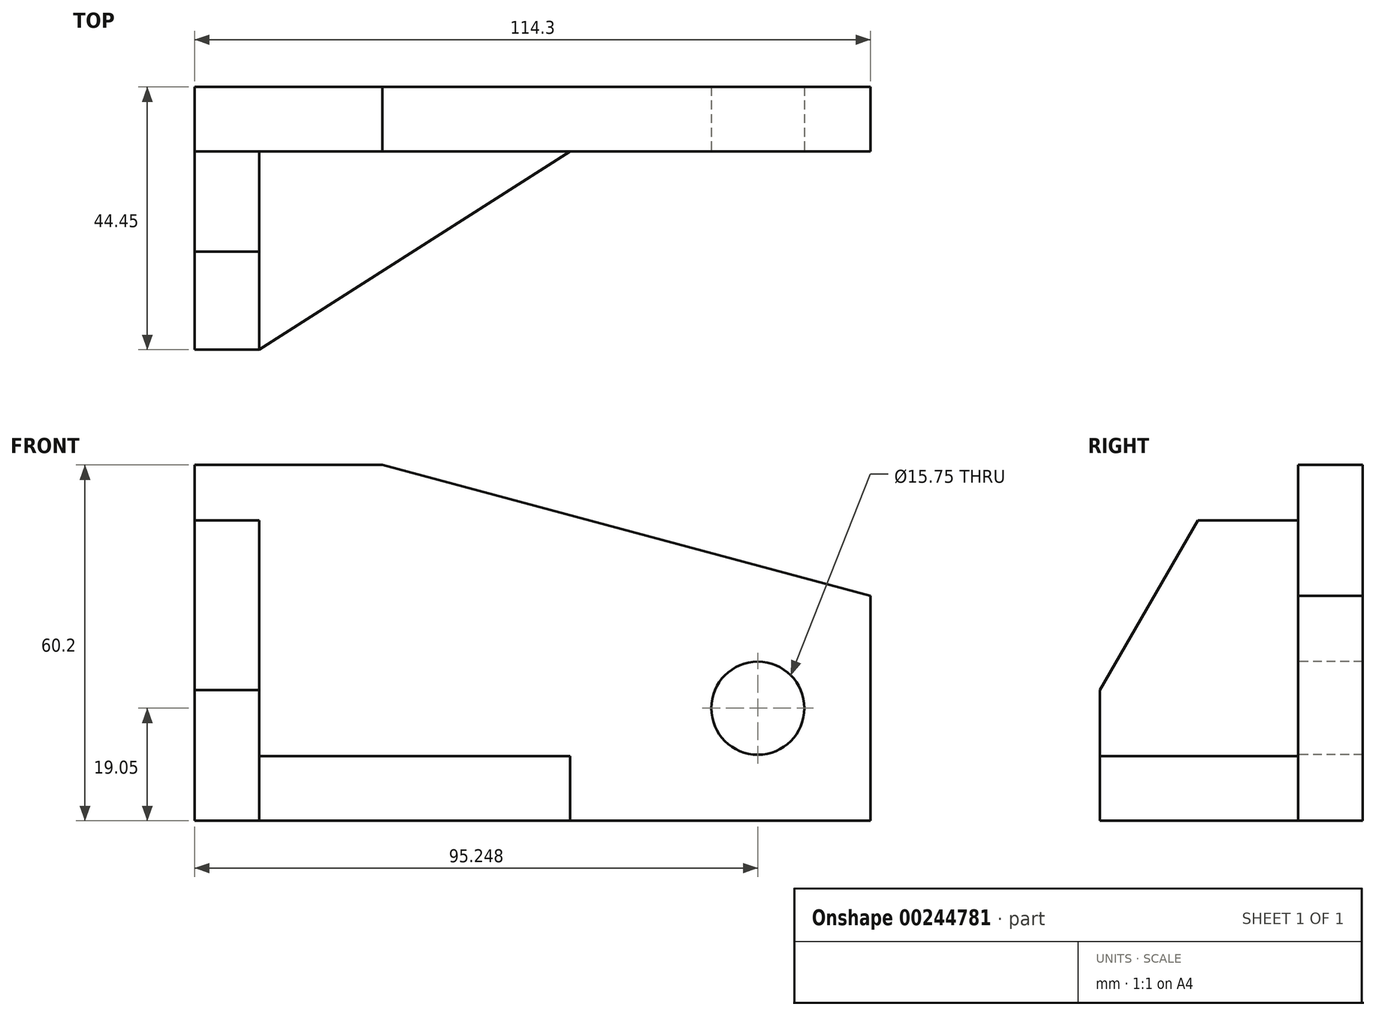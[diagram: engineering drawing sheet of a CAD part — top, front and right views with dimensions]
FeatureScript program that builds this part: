
annotation { "Feature Type Name" : "Feature", "Feature Type Description" : "" }
export const myFeature = defineFeature(function(context is Context, id is Id, definition is map)
    precondition{}
    {
        {
            var Q0;
            Q0=qCreatedBy(makeId("Front.planeOp"),FACE);
            var sketch = newSketch(context, id + "F0", { "sketchPlane" : qUnion([Q0])});
            skLineSegment(sketch, "E0.bottom", {"start": v(-10.92, 60.2) * mm, "end": v(20.83, 60.2) * mm});
            skLineSegment(sketch, "E0.top", {"start": v(-10.92, 0) * mm, "end": v(20.83, 0) * mm});
            skLineSegment(sketch, "E0.left", {"start": v(-10.92, 60.2) * mm, "end": v(-10.92, 0) * mm});
            skLineSegment(sketch, "E1", {"start": v(20.83, 60.2) * mm, "end": v(103.38, 38.08) * mm});
            skLineSegment(sketch, "E2", {"start": v(20.83, 0) * mm, "end": v(103.38, 0) * mm});
            skLineSegment(sketch, "E3", {"start": v(103.38, 38.08) * mm, "end": v(103.38, 0) * mm});
            skSolve(sketch);
        }
        {
            var Q0;
            Q0 = qSketchRegion(id + "F0", true);
            extrude(context, id + "F1", {"entities" : qUnion([Q0]), "oppositeDirection" : true, "depth" : 10.92 * mm});
        }
        {
            var Q0;
            Q0=makeQuery(id+"F1.opExtrude","CAP_FACE",FACE,{"disambiguationData":[OSD([sQuery(id+"F0.wireOp",EDGE,"E0.bottom"),sQuery(id+"F0.wireOp",EDGE,"E0.top"),sQuery(id+"F0.wireOp",EDGE,"E0.left"),sQuery(id+"F0.wireOp",EDGE,"E1"),sQuery(id+"F0.wireOp",EDGE,"E2"),sQuery(id+"F0.wireOp",EDGE,"E3")])],"isStart":false});
            var sketch = newSketch(context, id + "F2", { "sketchPlane" : qUnion([Q0])});
            skCircle(sketch, "E4", {"center": v(-122.43, 19.05) * mm, "radius": 7.87 * mm});
            skSolve(sketch);
        }
        {
            var Q0;
            Q0 = qSketchRegion(id + "F2", true);
            extrude(context, id + "F3", {"entities" : qUnion([Q0]), "operationType" : NewBodyOperationType.REMOVE, "endBound" : BoundingType.THROUGH_ALL, "oppositeDirection" : true, "depth" : 25.4 * mm});
        }
        {
            var Q0;
            Q0=qCreatedBy(makeId("Right.planeOp"),FACE);
            var sketch = newSketch(context, id + "F4", { "sketchPlane" : qUnion([Q0])});
            skLineSegment(sketch, "E5", {"start": v(0, 0) * mm, "end": v(0, 50.8) * mm});
            skLineSegment(sketch, "E6", {"start": v(0, 50.8) * mm, "end": v(-16.96, 50.8) * mm});
            skLineSegment(sketch, "E7", {"start": v(-33.53, 22.1) * mm, "end": v(-16.96, 50.8) * mm});
            skLineSegment(sketch, "E8", {"start": v(-33.53, 22.1) * mm, "end": v(-33.53, 0) * mm});
            skLineSegment(sketch, "E9", {"start": v(-33.53, 0) * mm, "end": v(0, 0) * mm});
            skSolve(sketch);
        }
        {
            var Q0;
            Q0=makeQuery(id+"F4.imprint","IMPRINT",FACE,{"disambiguationData":[TD([[makeQuery(id+"F4.imprint","IMPRINT",EDGE,{"derivedFrom":sQuery(id+"F4.wireOp",EDGE,"E5")}),1.0]])]});
            extrude(context, id + "F5", {"entities" : qUnion([Q0]), "operationType" : NewBodyOperationType.ADD, "oppositeDirection" : true, "depth" : 10.92 * mm});
        }
        {
            var Q0;
            Q0=qCreatedBy(makeId("Top.planeOp"),FACE);
            var sketch = newSketch(context, id + "F6", { "sketchPlane" : qUnion([Q0])});
            skLineSegment(sketch, "E10", {"start": v(0, 0) * mm, "end": v(0, -33.53) * mm});
            skLineSegment(sketch, "E11", {"start": v(0, -33.53) * mm, "end": v(52.58, 0) * mm});
            skLineSegment(sketch, "E12", {"start": v(52.58, 0) * mm, "end": v(0, 0) * mm});
            skSolve(sketch);
        }
        {
            var Q0;
            Q0 = qSketchRegion(id + "F6", true);
            extrude(context, id + "F7", {"entities" : qUnion([Q0]), "operationType" : NewBodyOperationType.ADD, "depth" : 10.92 * mm});
        }
        {
            var Q0;
            Q0=makeQuery(id+"F1.opExtrude","CAP_FACE",FACE,{"disambiguationData":[OSD([sQuery(id+"F0.wireOp",EDGE,"E0.bottom"),sQuery(id+"F0.wireOp",EDGE,"E0.top"),sQuery(id+"F0.wireOp",EDGE,"E0.left"),sQuery(id+"F0.wireOp",EDGE,"E1"),sQuery(id+"F0.wireOp",EDGE,"E2"),sQuery(id+"F0.wireOp",EDGE,"E3")])],"isStart":true});
            var sketch = newSketch(context, id + "F8", { "sketchPlane" : qUnion([Q0])});
            skCircle(sketch, "E13", {"center": v(84.33, 19.05) * mm, "radius": 7.87 * mm});
            skSolve(sketch);
        }
        {
            var Q0;
            Q0 = qSketchRegion(id + "F8", true);
            extrude(context, id + "F9", {"entities" : qUnion([Q0]), "operationType" : NewBodyOperationType.REMOVE, "endBound" : BoundingType.THROUGH_ALL, "oppositeDirection" : true, "depth" : 25.4 * mm});
        }
    });
